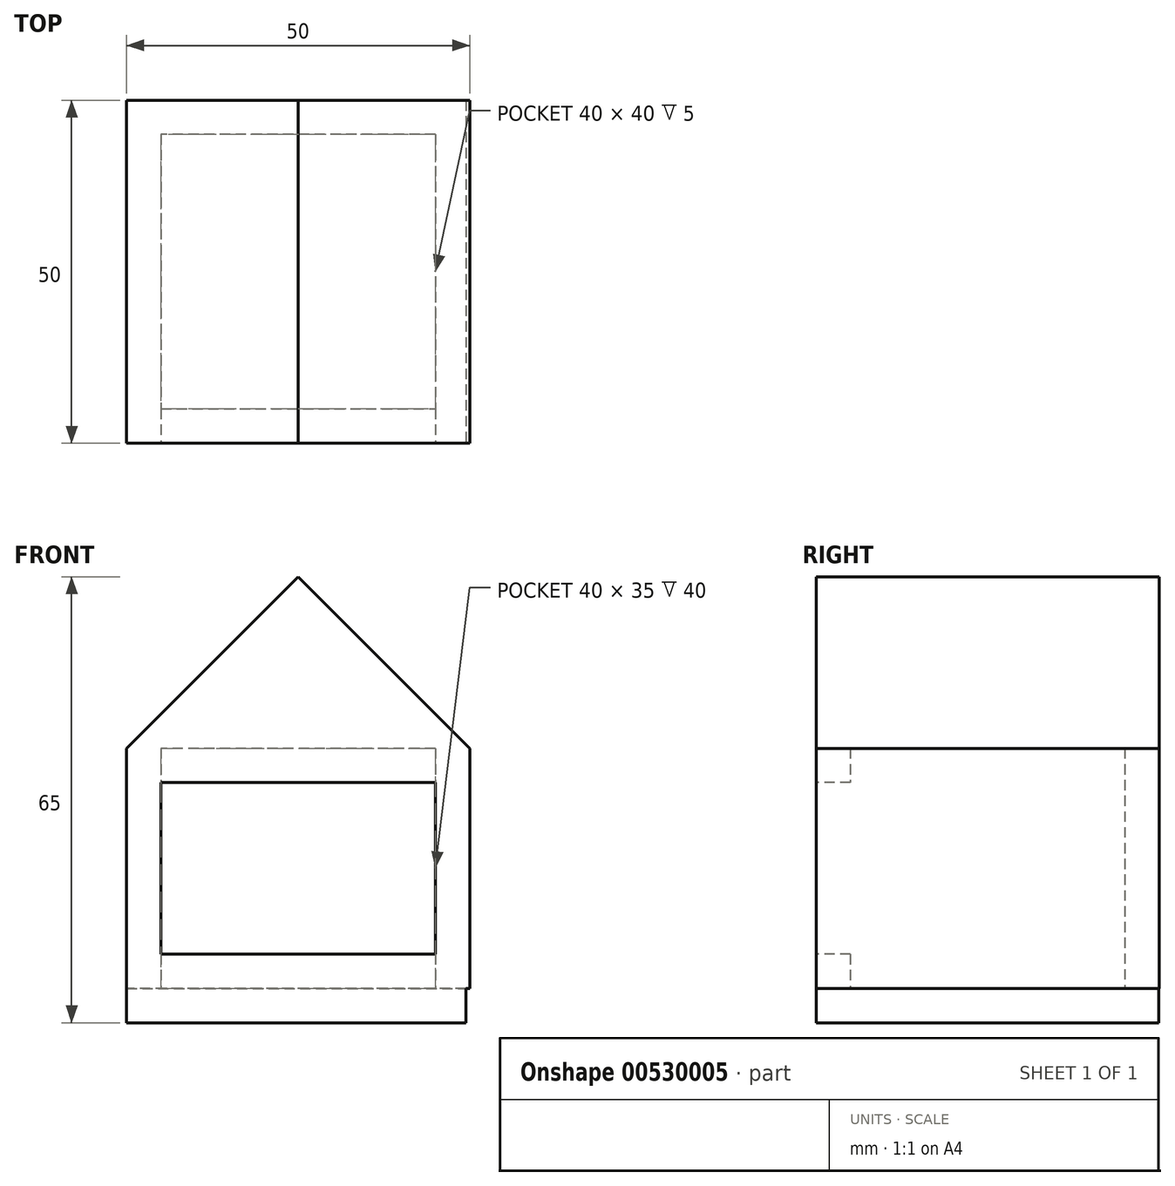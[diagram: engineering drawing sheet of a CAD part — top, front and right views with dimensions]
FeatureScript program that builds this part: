
annotation { "Feature Type Name" : "Feature", "Feature Type Description" : "" }
export const myFeature = defineFeature(function(context is Context, id is Id, definition is map)
    precondition{}
    {
        {
            var Q0;
            Q0=qCreatedBy(makeId("Top.planeOp"),FACE);
            var sketch = newSketch(context, id + "F0", { "sketchPlane" : qUnion([Q0])});
            skLineSegment(sketch, "E0.bottom", {"start": v(0, 0) * mm, "end": v(50, 0) * mm});
            skLineSegment(sketch, "E0.top", {"start": v(0, 50) * mm, "end": v(50, 50) * mm});
            skLineSegment(sketch, "E0.left", {"start": v(0, 0) * mm, "end": v(0, 50) * mm});
            skLineSegment(sketch, "E0.right", {"start": v(50, 0) * mm, "end": v(50, 50) * mm});
            skLineSegment(sketch, "E1.bottom", {"start": v(45, 45) * mm, "end": v(5, 45) * mm});
            skLineSegment(sketch, "E1.top", {"start": v(45, 5) * mm, "end": v(5, 5) * mm});
            skLineSegment(sketch, "E1.left", {"start": v(45, 45) * mm, "end": v(45, 5) * mm});
            skLineSegment(sketch, "E1.right", {"start": v(5, 45) * mm, "end": v(5, 5) * mm});
            skPoint(sketch, "E1.middle", {"position": v(25, 25) * mm});
            skLineSegment(sketch, "E2", {"start": v(25, 25) * mm, "end": v(25, 50) * mm, "construction": true});
            skLineSegment(sketch, "E3", {"start": v(25, 25) * mm, "end": v(0, 25) * mm, "construction": true});
            skSolve(sketch);
        }
        {
            var Q0;
            Q0 = qSketchRegion(id + "F0", true);
            extrude(context, id + "F1", {"entities" : qUnion([Q0]), "depth" : 35 * mm, "offsetDistance" : 25 * mm});
        }
        {
            var Q0;
            Q0=makeQuery(id+"F1.opExtrude","CAP_FACE",FACE,{"disambiguationData":[OSD([sQuery(id+"F0.wireOp",EDGE,"E0.bottom"),sQuery(id+"F0.wireOp",EDGE,"E0.top"),sQuery(id+"F0.wireOp",EDGE,"E0.left"),sQuery(id+"F0.wireOp",EDGE,"E0.right"),sQuery(id+"F0.wireOp",EDGE,"E1.bottom"),sQuery(id+"F0.wireOp",EDGE,"E1.top"),sQuery(id+"F0.wireOp",EDGE,"E1.left"),sQuery(id+"F0.wireOp",EDGE,"E1.right")])],"isStart":false});
            var sketch = newSketch(context, id + "F2", { "sketchPlane" : qUnion([Q0])});
            skLineSegment(sketch, "E4.bottom", {"start": v(0, 50) * mm, "end": v(50, 50) * mm});
            skLineSegment(sketch, "E4.top", {"start": v(0, 0) * mm, "end": v(50, 0) * mm});
            skLineSegment(sketch, "E4.left", {"start": v(0, 50) * mm, "end": v(0, 0) * mm});
            skLineSegment(sketch, "E4.right", {"start": v(50, 50) * mm, "end": v(50, 0) * mm});
            skSolve(sketch);
        }
        {
            var Q0;
            Q0 = qSketchRegion(id + "F2", true);
            extrude(context, id + "F3", {"entities" : qUnion([Q0]), "operationType" : NewBodyOperationType.ADD, "depth" : 25 * mm, "offsetDistance" : 25 * mm});
        }
        {
            var Q0;
            Q0=makeQuery(id+"F3.opExtrude","CAP_EDGE",EDGE,{"disambiguationData":[OSD([sQuery(id+"F2.wireOp",EDGE,"E4.left")])],"isStart":false});
            var Q1;
            Q1=makeQuery(id+"F3.opExtrude","CAP_EDGE",EDGE,{"disambiguationData":[OSD([sQuery(id+"F2.wireOp",EDGE,"E4.right")])],"isStart":false});
            chamfer(context, id + "F4", {"entities" : qUnion([Q0, Q1]), "width" : 25 * mm, "tangentPropagation" : true});
        }
        {
            var Q0;
            Q0=makeQuery(id+"F3.boolean.opBoolean","MERGE",FACE,{"derivedFrom":[makeQuery(id+"F1.opExtrude","SWEPT_FACE",FACE,{"disambiguationData":[OSD([sQuery(id+"F0.wireOp",EDGE,"E0.bottom")])]}),makeQuery(id+"F3.opExtrude","SWEPT_FACE",FACE,{"disambiguationData":[OSD([sQuery(id+"F2.wireOp",EDGE,"E4.top")])]})]});
            var sketch = newSketch(context, id + "F5", { "sketchPlane" : qUnion([Q0])});
            skLineSegment(sketch, "E5.bottom", {"start": v(5, 5) * mm, "end": v(45, 5) * mm});
            skLineSegment(sketch, "E5.top", {"start": v(5, 30) * mm, "end": v(45, 30) * mm});
            skLineSegment(sketch, "E5.left", {"start": v(5, 5) * mm, "end": v(5, 30) * mm});
            skLineSegment(sketch, "E5.right", {"start": v(45, 5) * mm, "end": v(45, 30) * mm});
            skPoint(sketch, "E5.middle", {"position": v(25, 17.5) * mm});
            skLineSegment(sketch, "E6", {"start": v(25, 17.5) * mm, "end": v(0, 17.5) * mm, "construction": true});
            skLineSegment(sketch, "E7", {"start": v(25, 17.5) * mm, "end": v(25, 60) * mm, "construction": true});
            skSolve(sketch);
        }
        {
            var Q0;
            Q0 = qSketchRegion(id + "F5", true);
            extrude(context, id + "F6", {"entities" : qUnion([Q0]), "operationType" : NewBodyOperationType.REMOVE, "oppositeDirection" : true, "depth" : 35 * mm, "offsetDistance" : 25 * mm});
        }
        {
            var Q0;
            Q0=makeQuery(id+"F1.opExtrude","CAP_FACE",FACE,{"disambiguationData":[OSD([sQuery(id+"F0.wireOp",EDGE,"E0.bottom"),sQuery(id+"F0.wireOp",EDGE,"E0.top"),sQuery(id+"F0.wireOp",EDGE,"E0.left"),sQuery(id+"F0.wireOp",EDGE,"E0.right"),sQuery(id+"F0.wireOp",EDGE,"E1.bottom"),sQuery(id+"F0.wireOp",EDGE,"E1.top"),sQuery(id+"F0.wireOp",EDGE,"E1.left"),sQuery(id+"F0.wireOp",EDGE,"E1.right")])],"isStart":true});
            var sketch = newSketch(context, id + "F7", { "sketchPlane" : qUnion([Q0])});
            skLineSegment(sketch, "E8.bottom", {"start": v(0, 0) * mm, "end": v(50, 0) * mm});
            skLineSegment(sketch, "E8.top", {"start": v(0, -50) * mm, "end": v(50, -50) * mm});
            skLineSegment(sketch, "E8.left", {"start": v(0, 0) * mm, "end": v(0, -50) * mm});
            skLineSegment(sketch, "E8.right", {"start": v(50, 0) * mm, "end": v(50, -50) * mm});
            skSolve(sketch);
        }
        {
            var Q0;
            Q0 = qSketchRegion(id + "F7", true);
            var sketch = newSketch(context, id + "F8", { "sketchPlane" : qUnion([Q0])});
            skLineSegment(sketch, "E9.bottom", {"start": v(49.44, -49.95) * mm, "end": v(0, -49.95) * mm});
            skLineSegment(sketch, "E9.top", {"start": v(49.44, 0) * mm, "end": v(0, 0) * mm});
            skLineSegment(sketch, "E9.left", {"start": v(49.44, -49.95) * mm, "end": v(49.44, 0) * mm});
            skLineSegment(sketch, "E9.right", {"start": v(0, -49.95) * mm, "end": v(0, 0) * mm});
            skSolve(sketch);
        }
        {
            var Q0;
            Q0 = qSketchRegion(id + "F8", true);
            extrude(context, id + "F9", {"entities" : qUnion([Q0]), "operationType" : NewBodyOperationType.ADD, "depth" : 5 * mm, "offsetDistance" : 25 * mm});
        }
    });
